# Revit family: Firestop-Putty-STI-Series_SSP_Floor
name_source: partatom
category: Specialty Equipment
units: mm (PartAtom-declared; Revit-internal decimal feet)

## family parameters
Always vertical = Yes
Cut with Voids When Loaded = No
Enable Cutting in Views = No
Host = Floor
Maintain Annotation Orientation = No
OmniClass Number = 23.20.50.14.11
OmniClass Title = Penetrations Firestopping
Part Type = Normal
Room Calculation Point = No
Round Connector Dimension = Use Diameter
Shared = No

## types (1)
- Firestop-Putty-STI-Series_SSP_Floor
    Assembly Code = D4030900
    Color = Red
    Default Elevation = 0' - 0"
    Description = SpecSeal® Series SSP Intumescent Firestop Putty
    Fire Rating = Up to 4 Hr
    Firestopping-STI-Intumescent-red = STI Molded Intumescent
    Guide Specification = http://www.stifirestop.com
    Locate Distributor = http://www.stifirestop.com
    MSDS = http://files.systems.stifirestop.com
    Manufacturer = Specified Technologies Inc.
    Manufacturer Fax No. = 908.526.9623
    Model = Series SSP Putty
    Open Diameter = 2' - 2"
    Pipe OD = 2' - 0"
    Product Documentation Link = http://files.systems.stifirestop.com
    Product Page URL = http://www.stifirestop.com
    Seal depth = 0' - 0 1/2"
    Tested Systems = http://sti.fmpdata.net
    URL = http://www.stifirestop.com

## geometry (parser evidence)
native form markers: Blend x4, Sweep x2
no freeform markers — native parametric forms only
